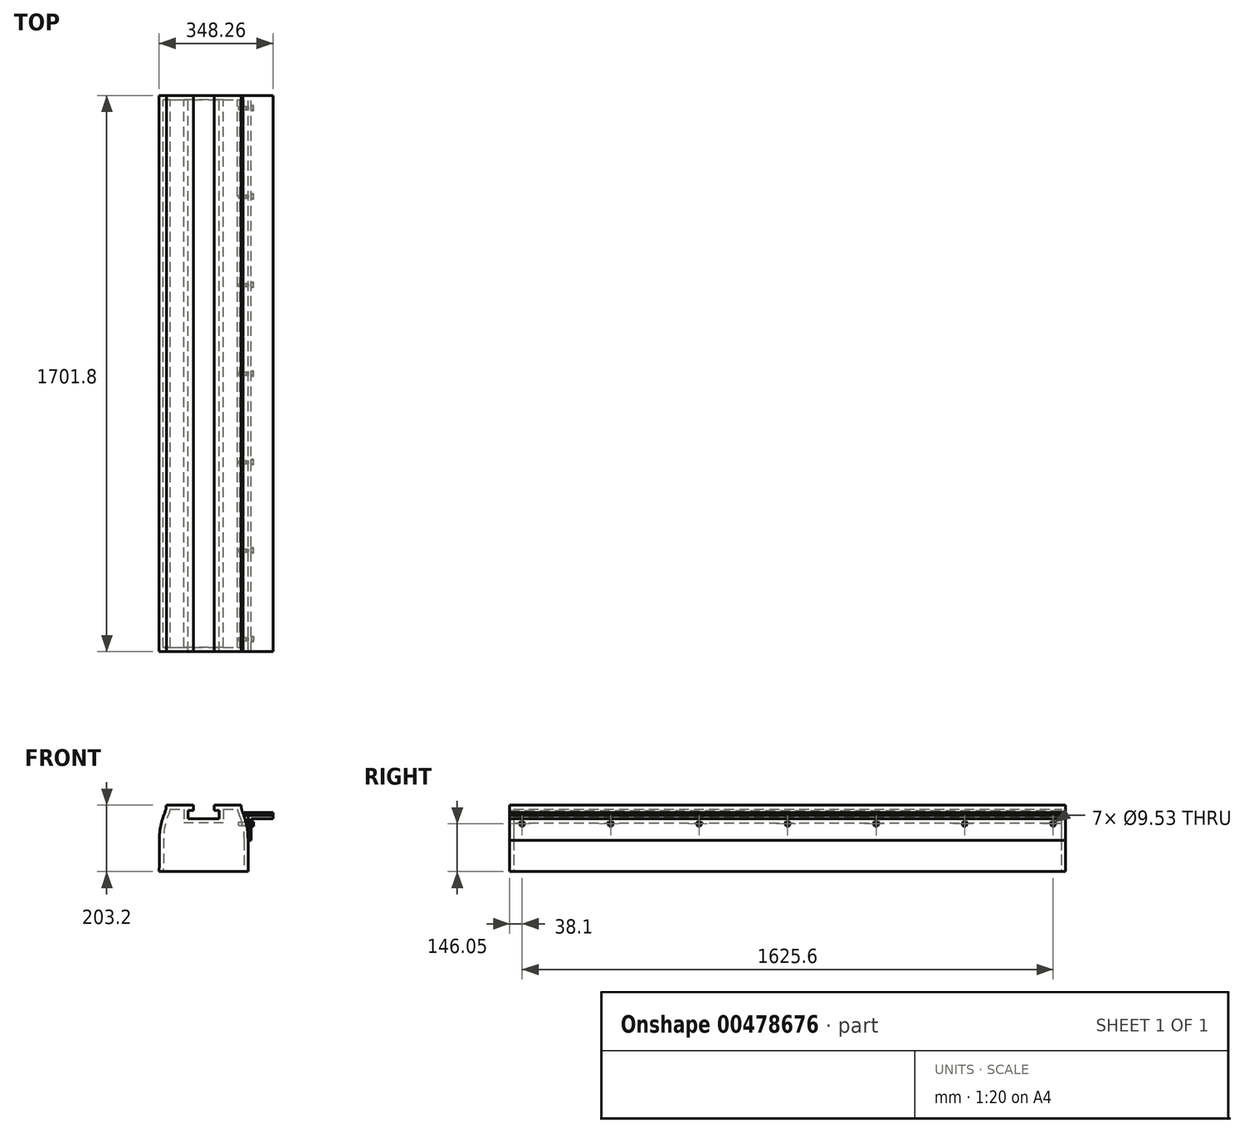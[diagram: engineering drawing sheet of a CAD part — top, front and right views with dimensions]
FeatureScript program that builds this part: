
annotation { "Feature Type Name" : "Feature", "Feature Type Description" : "" }
export const myFeature = defineFeature(function(context is Context, id is Id, definition is map)
    precondition{}
    {
        {
            var Q0;
            Q0=qCreatedBy(makeId("Front.planeOp"),FACE);
            var sketch = newSketch(context, id + "F0", { "sketchPlane" : qUnion([Q0])});
            skLineSegment(sketch, "E0.bottom", {"start": v(0, 0) * mm, "end": v(136.53, 0) * mm});
            skLineSegment(sketch, "E0.top", {"start": v(22.23, 203.2) * mm, "end": v(104.78, 203.2) * mm});
            skLineSegment(sketch, "E1.left", {"start": v(-15.88, 0) * mm, "end": v(-15.88, 203.2) * mm, "construction": true});
            skPoint(sketch, "E2", {"position": v(22.23, 203.2) * mm});
            skPoint(sketch, "E3", {"position": v(20.52, 190.5) * mm});
            skPoint(sketch, "E4", {"position": v(16.18, 177.8) * mm});
            skPoint(sketch, "E5", {"position": v(11.43, 165.1) * mm});
            skPoint(sketch, "E6", {"position": v(8.2, 152.4) * mm});
            skPoint(sketch, "E7", {"position": v(4.98, 139.7) * mm});
            skPoint(sketch, "E8", {"position": v(2.49, 127) * mm});
            skPoint(sketch, "E9", {"position": v(1.37, 114.3) * mm});
            skPoint(sketch, "E10", {"position": v(1.07, 101.6) * mm});
            skFitSpline(sketch, "E11", {"points": [v(22.23, 203.2) * mm, v(20.52, 190.5) * mm, v(16.18, 177.8) * mm, v(11.43, 165.1) * mm, v(8.2, 152.4) * mm, v(4.98, 139.7) * mm, v(2.49, 127) * mm, v(1.37, 114.3) * mm, v(1.07, 101.6) * mm, v(0, 0) * mm], "startDerivative": vector(-11.78, -139.04) * mm, "endDerivative": vector(-5, -490.08) * mm});
            skPoint(sketch, "E12", {"position": v(136.53, 0) * mm});
            skLineSegment(sketch, "E13", {"start": v(136.52, 203.2) * mm, "end": v(136.52, 0) * mm, "construction": true});
            skFitSpline(sketch, "E14.MirrorCS", {"points": [v(250.82, 203.2) * mm, v(252.53, 190.5) * mm, v(256.87, 177.8) * mm, v(261.62, 165.1) * mm, v(264.86, 152.4) * mm, v(268.07, 139.7) * mm, v(270.56, 127) * mm, v(271.68, 114.3) * mm, v(271.98, 101.6) * mm, v(273.05, 0) * mm], "startDerivative": vector(11.78, -139.04) * mm, "endDerivative": vector(5, -490.08) * mm});
            skLineSegment(sketch, "E15.MirrorCS", {"start": v(273.05, 0) * mm, "end": v(136.53, 0) * mm});
            skPoint(sketch, "E16.middle", {"position": v(136.52, 203.2) * mm});
            skLineSegment(sketch, "E17", {"start": v(104.78, 203.2) * mm, "end": v(104.78, 187.33) * mm});
            skLineSegment(sketch, "E18", {"start": v(104.78, 187.33) * mm, "end": v(88.9, 187.33) * mm});
            skLineSegment(sketch, "E19", {"start": v(88.9, 187.33) * mm, "end": v(88.9, 161.93) * mm});
            skLineSegment(sketch, "E20", {"start": v(88.9, 161.93) * mm, "end": v(136.52, 161.93) * mm});
            skLineSegment(sketch, "E21.MirrorCS", {"start": v(184.15, 187.33) * mm, "end": v(184.15, 161.93) * mm});
            skLineSegment(sketch, "E22.MirrorCS", {"start": v(184.15, 161.93) * mm, "end": v(136.53, 161.93) * mm});
            skLineSegment(sketch, "E23.MirrorCS", {"start": v(168.28, 187.33) * mm, "end": v(184.15, 187.33) * mm});
            skLineSegment(sketch, "E24.MirrorCS", {"start": v(168.28, 203.2) * mm, "end": v(168.28, 187.33) * mm});
            skPoint(sketch, "E25", {"position": v(104.78, 203.2) * mm});
            skPoint(sketch, "E26", {"position": v(168.28, 203.2) * mm});
            skLineSegment(sketch, "E27", {"start": v(168.28, 203.2) * mm, "end": v(250.83, 203.2) * mm});
            skLineSegment(sketch, "E28", {"start": v(0, 0) * mm, "end": v(2.5, 237.7) * mm, "construction": true});
            skLineSegment(sketch, "E29", {"start": v(272.06, 171.45) * mm, "end": v(272.06, 95.25) * mm});
            skLineSegment(sketch, "E30", {"start": v(272.06, 95.25) * mm, "end": v(281.58, 95.25) * mm});
            skLineSegment(sketch, "E31", {"start": v(281.58, 95.25) * mm, "end": v(281.58, 161.93) * mm});
            skLineSegment(sketch, "E32", {"start": v(281.58, 161.93) * mm, "end": v(348.26, 161.93) * mm});
            skLineSegment(sketch, "E33", {"start": v(348.26, 161.93) * mm, "end": v(348.26, 171.45) * mm});
            skLineSegment(sketch, "E34", {"start": v(348.26, 171.45) * mm, "end": v(272.06, 171.45) * mm});
            skLineSegment(sketch, "E35.right", {"start": v(348.26, 180.98) * mm, "end": v(348.26, 171.45) * mm});
            skLineSegment(sketch, "E36.trimOffspring", {"start": v(259.4, 171.45) * mm, "end": v(348.26, 171.45) * mm});
            skLineSegment(sketch, "E37", {"start": v(348.26, 180.98) * mm, "end": v(255.61, 180.98) * mm});
            skLineSegment(sketch, "E38", {"start": v(255.61, 180.98) * mm, "end": v(259.4, 171.45) * mm});
            skSolve(sketch);
        }
        {
            var Q0;
            Q0=makeQuery(id+"F0.imprint","IMPRINT",FACE,{"disambiguationData":[TD([[makeQuery(id+"F0.imprint","IMPRINT",EDGE,{"derivedFrom":sQuery(id+"F0.wireOp",EDGE,"E0.bottom")}),1.0]])]});
            extrude(context, id + "F1", {"entities" : qUnion([Q0]), "depth" : 1701.8 * mm, "offsetDistance" : 25.4 * mm});
        }
        {
            var Q0;
            Q0=makeQuery(id+"F1.opExtrude","SWEPT_FACE",FACE,{"disambiguationData":[OSD([sQuery(id+"F0.wireOp",EDGE,"E0.bottom"),sQuery(id+"F0.wireOp",EDGE,"E15.MirrorCS")])]});
            shell(context, id + "F2", {"entities" : qUnion([Q0]), "thickness" : 12.7 * mm});
        }
        {
            var Q0;
            {var subQ5=sQuery(id+"F0.wireOp",EDGE,"E35.right");Q0=makeQuery(id+"F0.imprint","IMPRINT",FACE,{"disambiguationData":[TD([[makeQuery(id+"F0.imprint","IMPRINT",EDGE,{"derivedFrom":subQ5}),-1.0]])]});}
            extrude(context, id + "F3", {"entities" : qUnion([Q0]), "depth" : 1701.8 * mm, "offsetDistance" : 25.4 * mm});
        }
        {
            var Q0;
            {var subQ0=sQuery(id+"F0.wireOp",EDGE,"E29");Q0=makeQuery(id+"F0.imprint","IMPRINT",FACE,{"disambiguationData":[TD([[makeQuery(id+"F0.imprint","IMPRINT",EDGE,{"derivedFrom":subQ0}),1.0]])]});}
            extrude(context, id + "F4", {"entities" : qUnion([Q0]), "depth" : 1701.8 * mm, "offsetDistance" : 25.4 * mm});
        }
        {
            var Q0;
            Q0=makeQuery(id+"F4.opExtrude","SWEPT_FACE",FACE,{"disambiguationData":[OSD([sQuery(id+"F0.wireOp",EDGE,"E31")])]});
            var sketch = newSketch(context, id + "F5", { "sketchPlane" : qUnion([Q0])});
            skLineSegment(sketch, "E39", {"start": v(-1701.8, 146.05) * mm, "end": v(0, 146.05) * mm, "construction": true});
            skCircle(sketch, "E40", {"center": v(-1663.7, 146.05) * mm, "radius": 4.76 * mm});
            skCircle(sketch, "E41.1.0.0", {"center": v(-1392.77, 146.05) * mm, "radius": 4.76 * mm});
            skCircle(sketch, "E41.2.0.0", {"center": v(-1121.83, 146.05) * mm, "radius": 4.76 * mm});
            skCircle(sketch, "E41.3.0.0", {"center": v(-850.9, 146.05) * mm, "radius": 4.76 * mm});
            skCircle(sketch, "E41.4.0.0", {"center": v(-579.97, 146.05) * mm, "radius": 4.76 * mm});
            skCircle(sketch, "E41.5.0.0", {"center": v(-309.03, 146.05) * mm, "radius": 4.76 * mm});
            skCircle(sketch, "E41.6.0.0", {"center": v(-38.1, 146.05) * mm, "radius": 4.76 * mm});
            skLineSegment(sketch, "E41.direction1", {"start": v(-1663.7, 146.05) * mm, "end": v(-1392.77, 146.05) * mm, "construction": true});
            skSolve(sketch);
        }
        {
            var Q0;
            Q0 = qSketchRegion(id + "F5", true);
            extrude(context, id + "F6", {"entities" : qUnion([Q0]), "operationType" : NewBodyOperationType.REMOVE, "oppositeDirection" : true, "depth" : 76.2 * mm, "offsetDistance" : 25.4 * mm});
        }
        {
            var Q0;
            Q0=makeQuery(id+"F4.opExtrude","SWEPT_FACE",FACE,{"disambiguationData":[OSD([sQuery(id+"F0.wireOp",EDGE,"E31")])]});
            var sketch = newSketch(context, id + "F7", { "sketchPlane" : qUnion([Q0])});
            skCircle(sketch, "E42", {"center": v(-1663.7, 146.05) * mm, "radius": 4.76 * mm});
            skCircle(sketch, "E43.cCircle", {"center": v(-1663.7, 146.05) * mm, "radius": 7.14 * mm, "construction": true});
            skLineSegment(sketch, "E43.0", {"start": v(-1659.58, 138.9) * mm, "end": v(-1667.82, 138.9) * mm});
            skLineSegment(sketch, "E43.1", {"start": v(-1667.82, 138.9) * mm, "end": v(-1671.95, 146.05) * mm});
            skLineSegment(sketch, "E43.2", {"start": v(-1671.95, 146.05) * mm, "end": v(-1667.82, 153.2) * mm});
            skLineSegment(sketch, "E43.3", {"start": v(-1667.82, 153.2) * mm, "end": v(-1659.58, 153.2) * mm});
            skLineSegment(sketch, "E43.4", {"start": v(-1659.58, 153.2) * mm, "end": v(-1655.45, 146.05) * mm});
            skLineSegment(sketch, "E43.5", {"start": v(-1655.45, 146.05) * mm, "end": v(-1659.58, 138.9) * mm});
            skPoint(sketch, "E43.0.midPoint", {"position": v(-1663.7, 138.9) * mm});
            skLineSegment(sketch, "E44.1.0.0", {"start": v(-1388.64, 153.2) * mm, "end": v(-1384.52, 146.05) * mm});
            skLineSegment(sketch, "E44.1.0.1", {"start": v(-1384.52, 146.05) * mm, "end": v(-1388.64, 138.9) * mm});
            skLineSegment(sketch, "E44.1.0.2", {"start": v(-1388.64, 138.9) * mm, "end": v(-1396.9, 138.9) * mm});
            skLineSegment(sketch, "E44.1.0.3", {"start": v(-1396.9, 138.9) * mm, "end": v(-1401.02, 146.05) * mm});
            skLineSegment(sketch, "E44.1.0.4", {"start": v(-1401.02, 146.05) * mm, "end": v(-1396.9, 153.2) * mm});
            skLineSegment(sketch, "E44.1.0.5", {"start": v(-1396.9, 153.2) * mm, "end": v(-1388.64, 153.2) * mm});
            skCircle(sketch, "E44.1.0.6", {"center": v(-1392.77, 146.05) * mm, "radius": 4.76 * mm});
            skLineSegment(sketch, "E44.2.0.0", {"start": v(-1117.7, 153.2) * mm, "end": v(-1113.58, 146.05) * mm});
            skLineSegment(sketch, "E44.2.0.1", {"start": v(-1113.58, 146.05) * mm, "end": v(-1117.7, 138.9) * mm});
            skLineSegment(sketch, "E44.2.0.2", {"start": v(-1117.7, 138.9) * mm, "end": v(-1125.96, 138.9) * mm});
            skLineSegment(sketch, "E44.2.0.3", {"start": v(-1125.96, 138.9) * mm, "end": v(-1130.08, 146.05) * mm});
            skLineSegment(sketch, "E44.2.0.4", {"start": v(-1130.08, 146.05) * mm, "end": v(-1125.96, 153.2) * mm});
            skLineSegment(sketch, "E44.2.0.5", {"start": v(-1125.96, 153.2) * mm, "end": v(-1117.7, 153.2) * mm});
            skCircle(sketch, "E44.2.0.6", {"center": v(-1121.83, 146.05) * mm, "radius": 4.76 * mm});
            skLineSegment(sketch, "E44.3.0.0", {"start": v(-846.78, 153.2) * mm, "end": v(-842.65, 146.05) * mm});
            skLineSegment(sketch, "E44.3.0.1", {"start": v(-842.65, 146.05) * mm, "end": v(-846.78, 138.9) * mm});
            skLineSegment(sketch, "E44.3.0.2", {"start": v(-846.78, 138.9) * mm, "end": v(-855.02, 138.9) * mm});
            skLineSegment(sketch, "E44.3.0.3", {"start": v(-855.02, 138.9) * mm, "end": v(-859.15, 146.05) * mm});
            skLineSegment(sketch, "E44.3.0.4", {"start": v(-859.15, 146.05) * mm, "end": v(-855.02, 153.2) * mm});
            skLineSegment(sketch, "E44.3.0.5", {"start": v(-855.02, 153.2) * mm, "end": v(-846.78, 153.2) * mm});
            skCircle(sketch, "E44.3.0.6", {"center": v(-850.9, 146.05) * mm, "radius": 4.76 * mm});
            skLineSegment(sketch, "E44.4.0.0", {"start": v(-575.84, 153.2) * mm, "end": v(-571.72, 146.05) * mm});
            skLineSegment(sketch, "E44.4.0.1", {"start": v(-571.72, 146.05) * mm, "end": v(-575.84, 138.9) * mm});
            skLineSegment(sketch, "E44.4.0.2", {"start": v(-575.84, 138.9) * mm, "end": v(-584.1, 138.9) * mm});
            skLineSegment(sketch, "E44.4.0.3", {"start": v(-584.1, 138.9) * mm, "end": v(-588.22, 146.05) * mm});
            skLineSegment(sketch, "E44.4.0.4", {"start": v(-588.22, 146.05) * mm, "end": v(-584.1, 153.2) * mm});
            skLineSegment(sketch, "E44.4.0.5", {"start": v(-584.1, 153.2) * mm, "end": v(-575.84, 153.2) * mm});
            skCircle(sketch, "E44.4.0.6", {"center": v(-579.97, 146.05) * mm, "radius": 4.76 * mm});
            skLineSegment(sketch, "E44.5.0.0", {"start": v(-304.9, 153.2) * mm, "end": v(-300.78, 146.05) * mm});
            skLineSegment(sketch, "E44.5.0.1", {"start": v(-300.78, 146.05) * mm, "end": v(-304.9, 138.9) * mm});
            skLineSegment(sketch, "E44.5.0.2", {"start": v(-304.9, 138.9) * mm, "end": v(-313.16, 138.9) * mm});
            skLineSegment(sketch, "E44.5.0.3", {"start": v(-313.16, 138.9) * mm, "end": v(-317.28, 146.05) * mm});
            skLineSegment(sketch, "E44.5.0.4", {"start": v(-317.28, 146.05) * mm, "end": v(-313.16, 153.2) * mm});
            skLineSegment(sketch, "E44.5.0.5", {"start": v(-313.16, 153.2) * mm, "end": v(-304.9, 153.2) * mm});
            skCircle(sketch, "E44.5.0.6", {"center": v(-309.03, 146.05) * mm, "radius": 4.76 * mm});
            skLineSegment(sketch, "E44.6.0.0", {"start": v(-33.98, 153.2) * mm, "end": v(-29.85, 146.05) * mm});
            skLineSegment(sketch, "E44.6.0.1", {"start": v(-29.85, 146.05) * mm, "end": v(-33.98, 138.9) * mm});
            skLineSegment(sketch, "E44.6.0.2", {"start": v(-33.98, 138.9) * mm, "end": v(-42.22, 138.9) * mm});
            skLineSegment(sketch, "E44.6.0.3", {"start": v(-42.22, 138.9) * mm, "end": v(-46.35, 146.05) * mm});
            skLineSegment(sketch, "E44.6.0.4", {"start": v(-46.35, 146.05) * mm, "end": v(-42.22, 153.2) * mm});
            skLineSegment(sketch, "E44.6.0.5", {"start": v(-42.22, 153.2) * mm, "end": v(-33.98, 153.2) * mm});
            skCircle(sketch, "E44.6.0.6", {"center": v(-38.1, 146.05) * mm, "radius": 4.76 * mm});
            skLineSegment(sketch, "E44.direction1", {"start": v(-1655.45, 146.05) * mm, "end": v(-1384.52, 146.05) * mm, "construction": true});
            skSolve(sketch);
        }
        {
            var Q0;
            Q0=makeQuery(id+"F7.imprint","IMPRINT",FACE,{"disambiguationData":[TD([[makeQuery(id+"F7.imprint","IMPRINT",EDGE,{"derivedFrom":sQuery(id+"F7.wireOp",EDGE,"E42")}),1.0]])]});
            var Q1;
            Q1=makeQuery(id+"F7.imprint","IMPRINT",FACE,{"disambiguationData":[TD([[makeQuery(id+"F7.imprint","IMPRINT",EDGE,{"derivedFrom":sQuery(id+"F7.wireOp",EDGE,"E44.1.0.6")}),1.0]])]});
            var Q2;
            Q2=makeQuery(id+"F7.imprint","IMPRINT",FACE,{"disambiguationData":[TD([[makeQuery(id+"F7.imprint","IMPRINT",EDGE,{"derivedFrom":sQuery(id+"F7.wireOp",EDGE,"E44.2.0.6")}),1.0]])]});
            var Q3;
            Q3=makeQuery(id+"F7.imprint","IMPRINT",FACE,{"disambiguationData":[TD([[makeQuery(id+"F7.imprint","IMPRINT",EDGE,{"derivedFrom":sQuery(id+"F7.wireOp",EDGE,"E44.3.0.6")}),1.0]])]});
            var Q4;
            Q4=makeQuery(id+"F7.imprint","IMPRINT",FACE,{"disambiguationData":[TD([[makeQuery(id+"F7.imprint","IMPRINT",EDGE,{"derivedFrom":sQuery(id+"F7.wireOp",EDGE,"E44.4.0.6")}),1.0]])]});
            var Q5;
            Q5=makeQuery(id+"F7.imprint","IMPRINT",FACE,{"disambiguationData":[TD([[makeQuery(id+"F7.imprint","IMPRINT",EDGE,{"derivedFrom":sQuery(id+"F7.wireOp",EDGE,"E44.5.0.6")}),1.0]])]});
            var Q6;
            Q6=makeQuery(id+"F7.imprint","IMPRINT",FACE,{"disambiguationData":[TD([[makeQuery(id+"F7.imprint","IMPRINT",EDGE,{"derivedFrom":sQuery(id+"F7.wireOp",EDGE,"E44.6.0.6")}),1.0]])]});
            extrude(context, id + "F8", {"entities" : qUnion([Q0, Q1, Q2, Q3, Q4, Q5, Q6]), "oppositeDirection" : true, "depth" : 38.1 * mm, "offsetDistance" : 25.4 * mm});
        }
        {
            var Q0;
            Q0 = qSketchRegion(id + "F7", true);
            var Q1;
            Q1=makeQuery(id+"F5.imprint","IMPRINT",FACE,{"disambiguationData":[TD([[makeQuery(id+"F5.imprint","IMPRINT",EDGE,{"derivedFrom":sQuery(id+"F5.wireOp",EDGE,"E40")}),1.0]])]});
            var Q2;
            Q2=makeQuery(id+"F5.imprint","IMPRINT",FACE,{"disambiguationData":[TD([[makeQuery(id+"F5.imprint","IMPRINT",EDGE,{"derivedFrom":sQuery(id+"F5.wireOp",EDGE,"E41.1.0.0")}),1.0]])]});
            var Q3;
            Q3=makeQuery(id+"F5.imprint","IMPRINT",FACE,{"disambiguationData":[TD([[makeQuery(id+"F5.imprint","IMPRINT",EDGE,{"derivedFrom":sQuery(id+"F5.wireOp",EDGE,"E41.2.0.0")}),1.0]])]});
            var Q4;
            Q4=makeQuery(id+"F5.imprint","IMPRINT",FACE,{"disambiguationData":[TD([[makeQuery(id+"F5.imprint","IMPRINT",EDGE,{"derivedFrom":sQuery(id+"F5.wireOp",EDGE,"E41.3.0.0")}),1.0]])]});
            var Q5;
            Q5=makeQuery(id+"F5.imprint","IMPRINT",FACE,{"disambiguationData":[TD([[makeQuery(id+"F5.imprint","IMPRINT",EDGE,{"derivedFrom":sQuery(id+"F5.wireOp",EDGE,"E41.4.0.0")}),1.0]])]});
            var Q6;
            Q6=makeQuery(id+"F5.imprint","IMPRINT",FACE,{"disambiguationData":[TD([[makeQuery(id+"F5.imprint","IMPRINT",EDGE,{"derivedFrom":sQuery(id+"F5.wireOp",EDGE,"E41.5.0.0")}),1.0]])]});
            var Q7;
            Q7=makeQuery(id+"F5.imprint","IMPRINT",FACE,{"disambiguationData":[TD([[makeQuery(id+"F5.imprint","IMPRINT",EDGE,{"derivedFrom":sQuery(id+"F5.wireOp",EDGE,"E41.6.0.0")}),1.0]])]});
            extrude(context, id + "F9", {"entities" : qUnion([Q0, Q1, Q2, Q3, Q4, Q5, Q6, Q7]), "operationType" : NewBodyOperationType.ADD, "depth" : 7.95 * mm, "offsetDistance" : 25.4 * mm});
        }
    });
